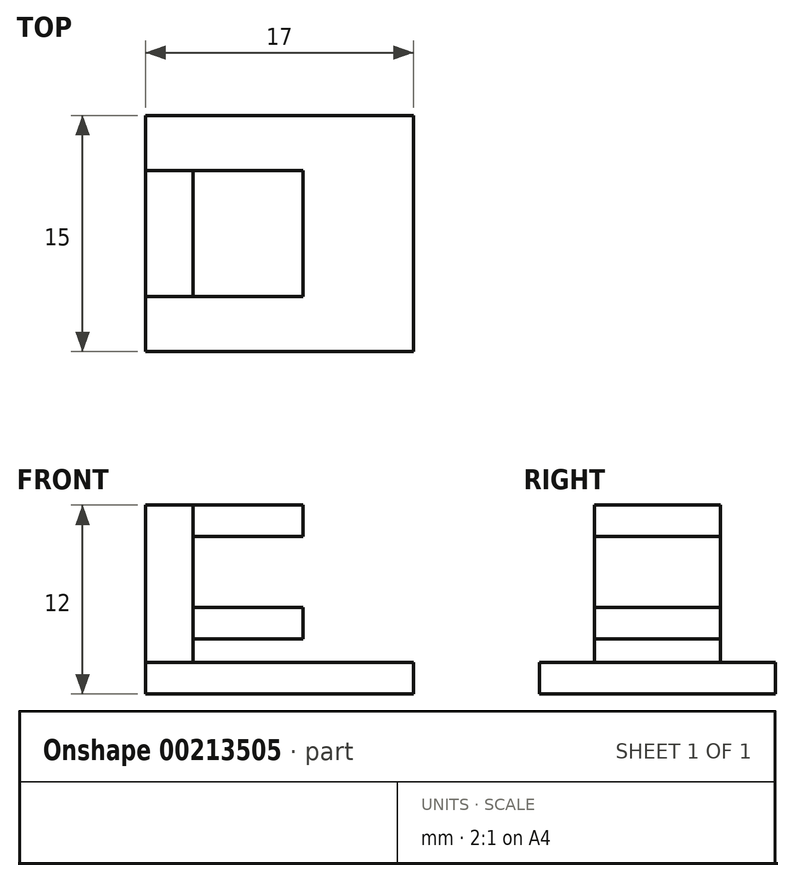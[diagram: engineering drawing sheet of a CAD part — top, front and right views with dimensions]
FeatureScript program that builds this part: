
annotation { "Feature Type Name" : "Feature", "Feature Type Description" : "" }
export const myFeature = defineFeature(function(context is Context, id is Id, definition is map)
    precondition{}
    {
        {
            var Q0;
            Q0=qCreatedBy(makeId("Top.planeOp"),FACE);
            var sketch = newSketch(context, id + "F0", { "sketchPlane" : qUnion([Q0])});
            skLineSegment(sketch, "E0", {"start": v(-39.3, -15) * mm, "end": v(-22.3, -15) * mm});
            skLineSegment(sketch, "E1", {"start": v(-22.3, -15) * mm, "end": v(-22.3, 0) * mm});
            skLineSegment(sketch, "E2", {"start": v(-39.3, -15) * mm, "end": v(-39.3, 0) * mm});
            skLineSegment(sketch, "E3", {"start": v(-39.3, 0) * mm, "end": v(-22.3, 0) * mm});
            skSolve(sketch);
        }
        {
            var Q0;
            Q0=makeQuery(id+"F0.imprint","IMPRINT",FACE,{"disambiguationData":[TD([[makeQuery(id+"F0.imprint","IMPRINT",EDGE,{"derivedFrom":sQuery(id+"F0.wireOp",EDGE,"E0")}),1.0]])]});
            extrude(context, id + "F1", {"entities" : qUnion([Q0]), "depth" : 2 * mm});
        }
        {
            var Q0;
            Q0=makeQuery(id+"F1.opExtrude","SWEPT_FACE",FACE,{"disambiguationData":[OSD([sQuery(id+"F0.wireOp",EDGE,"E2")])]});
            var sketch = newSketch(context, id + "F2", { "sketchPlane" : qUnion([Q0])});
            skLineSegment(sketch, "E4", {"start": v(7.5, 2) * mm, "end": v(3.5, 2) * mm});
            skLineSegment(sketch, "E5", {"start": v(7.5, 2) * mm, "end": v(11.5, 2) * mm});
            skPoint(sketch, "E6.end.orphan", {"position": v(7.5, 11) * mm});
            skLineSegment(sketch, "E7", {"start": v(3.5, 2) * mm, "end": v(3.5, 12) * mm});
            skPoint(sketch, "E8.start.orphan", {"position": v(3.5, 11) * mm});
            skPoint(sketch, "E9.end.orphan", {"position": v(11.5, 11) * mm});
            skLineSegment(sketch, "E10", {"start": v(11.5, 2) * mm, "end": v(11.5, 12) * mm});
            skLineSegment(sketch, "E11", {"start": v(3.5, 12) * mm, "end": v(11.5, 12) * mm});
            skSolve(sketch);
        }
        {
            var Q0;
            Q0=makeQuery(id+"F2.imprint","IMPRINT",FACE,{"disambiguationData":[TD([[makeQuery(id+"F2.imprint","IMPRINT",EDGE,{"derivedFrom":sQuery(id+"F2.wireOp",EDGE,"E4")}),-1.0]])]});
            extrude(context, id + "F3", {"entities" : qUnion([Q0]), "operationType" : NewBodyOperationType.ADD, "oppositeDirection" : true, "depth" : 3 * mm});
        }
        {
            var Q0;
            Q0=makeQuery(id+"F3.opExtrude","SWEPT_FACE",FACE,{"disambiguationData":[OSD([sQuery(id+"F2.wireOp",EDGE,"E7")])]});
            var sketch = newSketch(context, id + "F4", { "sketchPlane" : qUnion([Q0])});
            skLineSegment(sketch, "E12", {"start": v(36.3, 12) * mm, "end": v(36.3, 10) * mm});
            skLineSegment(sketch, "E13", {"start": v(36.3, 12) * mm, "end": v(29.3, 12) * mm});
            skLineSegment(sketch, "E14", {"start": v(29.3, 12) * mm, "end": v(29.3, 10) * mm});
            skLineSegment(sketch, "E15", {"start": v(29.3, 10) * mm, "end": v(36.3, 10) * mm});
            skLineSegment(sketch, "E16", {"start": v(36.3, 10) * mm, "end": v(36.3, 5.5) * mm});
            skLineSegment(sketch, "E17", {"start": v(36.3, 5.5) * mm, "end": v(29.3, 5.5) * mm});
            skLineSegment(sketch, "E18", {"start": v(29.3, 5.5) * mm, "end": v(29.3, 3.5) * mm});
            skLineSegment(sketch, "E19", {"start": v(29.3, 3.5) * mm, "end": v(36.3, 3.5) * mm});
            skSolve(sketch);
        }
        {
            var Q0;
            {var subQ0=sQuery(id+"F4.wireOp",EDGE,"E17");Q0=makeQuery(id+"F4.imprint","IMPRINT",FACE,{"disambiguationData":[TD([[makeQuery(id+"F4.imprint","IMPRINT",EDGE,{"derivedFrom":subQ0}),1.0]])]});}
            var Q1;
            Q1=makeQuery(id+"F4.imprint","IMPRINT",FACE,{"disambiguationData":[TD([[makeQuery(id+"F4.imprint","IMPRINT",EDGE,{"derivedFrom":sQuery(id+"F4.wireOp",EDGE,"E12")}),1.0]])]});
            extrude(context, id + "F5", {"entities" : qUnion([Q0, Q1]), "oppositeDirection" : true, "depth" : 8 * mm});
        }
    });
